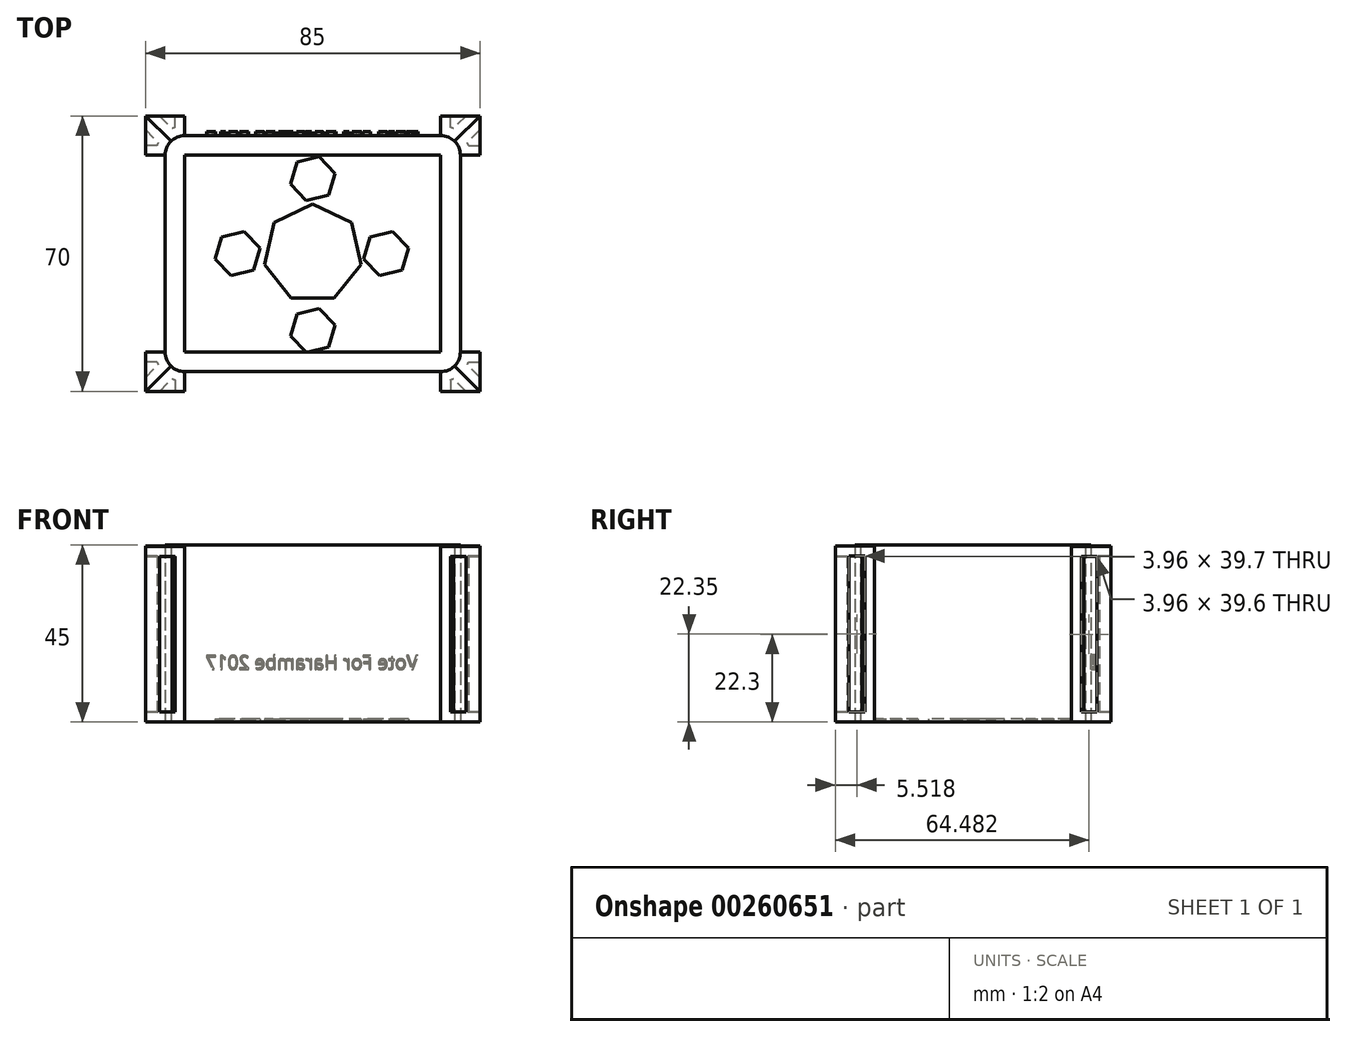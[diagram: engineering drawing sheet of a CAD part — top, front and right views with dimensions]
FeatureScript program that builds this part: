
annotation { "Feature Type Name" : "Feature", "Feature Type Description" : "" }
export const myFeature = defineFeature(function(context is Context, id is Id, definition is map)
    precondition{}
    {
        {
            var Q0;
            Q0=qCreatedBy(makeId("Top.planeOp"),FACE);
            var sketch = newSketch(context, id + "F0", { "sketchPlane" : qUnion([Q0])});
            skLineSegment(sketch, "E0.bottom", {"start": v(32.5, -30) * mm, "end": v(-32.5, -30) * mm});
            skLineSegment(sketch, "E0.top", {"start": v(32.5, 30) * mm, "end": v(-32.5, 30) * mm});
            skLineSegment(sketch, "E0.left", {"start": v(37.5, -25) * mm, "end": v(37.5, 25) * mm});
            skLineSegment(sketch, "E0.right", {"start": v(-37.5, -25) * mm, "end": v(-37.5, 25) * mm});
            skPoint(sketch, "E0.middle", {"position": v(0, 0) * mm});
            skLineSegment(sketch, "E1.bottom", {"start": v(32.5, -25) * mm, "end": v(-32.5, -25) * mm});
            skLineSegment(sketch, "E1.top", {"start": v(32.5, 25) * mm, "end": v(-32.5, 25) * mm});
            skLineSegment(sketch, "E1.left", {"start": v(32.5, -25) * mm, "end": v(32.5, 25) * mm});
            skLineSegment(sketch, "E1.right", {"start": v(-32.5, -25) * mm, "end": v(-32.5, 25) * mm});
            skPoint(sketch, "E2.middle", {"position": v(-37.5, 30) * mm});
            skPoint(sketch, "E3.visualSharp", {"position": v(37.5, 30) * mm});
            skArc(sketch, "E3.filletArc", {"start": v(37.5, 25) * mm, "mid": v(36.04, 28.54) * mm, "end": v(32.5, 30) * mm});
            skPoint(sketch, "E4.visualSharp", {"position": v(37.5, -30) * mm});
            skArc(sketch, "E4.filletArc", {"start": v(32.5, -30) * mm, "mid": v(36.04, -28.54) * mm, "end": v(37.5, -25) * mm});
            skPoint(sketch, "E5.visualSharp", {"position": v(-37.5, -30) * mm});
            skArc(sketch, "E5.filletArc", {"start": v(-37.5, -25) * mm, "mid": v(-36.04, -28.54) * mm, "end": v(-32.5, -30) * mm});
            skArc(sketch, "E6.filletArc", {"start": v(-32.5, 30) * mm, "mid": v(-36.04, 28.54) * mm, "end": v(-37.5, 25) * mm});
            skLineSegment(sketch, "E7.bottom", {"start": v(-32.5, 25) * mm, "end": v(-42.5, 25) * mm});
            skLineSegment(sketch, "E7.top", {"start": v(-32.5, 35) * mm, "end": v(-42.5, 35) * mm});
            skLineSegment(sketch, "E7.left", {"start": v(-32.5, 25) * mm, "end": v(-32.5, 35) * mm});
            skLineSegment(sketch, "E7.right", {"start": v(-42.5, 25) * mm, "end": v(-42.5, 35) * mm});
            skLineSegment(sketch, "E8.bottom", {"start": v(32.5, 25) * mm, "end": v(42.5, 25) * mm});
            skLineSegment(sketch, "E8.top", {"start": v(32.5, 35) * mm, "end": v(42.5, 35) * mm});
            skLineSegment(sketch, "E8.left", {"start": v(32.5, 25) * mm, "end": v(32.5, 35) * mm});
            skLineSegment(sketch, "E8.right", {"start": v(42.5, 25) * mm, "end": v(42.5, 35) * mm});
            skLineSegment(sketch, "E9.bottom", {"start": v(32.5, -25) * mm, "end": v(42.5, -25) * mm});
            skLineSegment(sketch, "E9.top", {"start": v(32.5, -35) * mm, "end": v(42.5, -35) * mm});
            skLineSegment(sketch, "E9.left", {"start": v(32.5, -25) * mm, "end": v(32.5, -35) * mm});
            skLineSegment(sketch, "E9.right", {"start": v(42.5, -25) * mm, "end": v(42.5, -35) * mm});
            skLineSegment(sketch, "E10.bottom", {"start": v(-32.5, -25) * mm, "end": v(-42.5, -25) * mm});
            skLineSegment(sketch, "E10.top", {"start": v(-32.5, -35) * mm, "end": v(-42.5, -35) * mm});
            skLineSegment(sketch, "E10.left", {"start": v(-32.5, -25) * mm, "end": v(-32.5, -35) * mm});
            skLineSegment(sketch, "E10.right", {"start": v(-42.5, -25) * mm, "end": v(-42.5, -35) * mm});
            skLineSegment(sketch, "E11", {"start": v(-42.5, 35) * mm, "end": v(-32.5, 25) * mm});
            skLineSegment(sketch, "E12", {"start": v(42.5, 35) * mm, "end": v(32.5, 25) * mm});
            skLineSegment(sketch, "E13", {"start": v(42.5, -35) * mm, "end": v(32.5, -25) * mm});
            skLineSegment(sketch, "E14", {"start": v(-42.5, -35) * mm, "end": v(-32.5, -25) * mm});
            skSolve(sketch);
        }
        {
            var Q0;
            {var subQ0=sQuery(id+"F0.wireOp",EDGE,"E0.bottom");Q0=makeQuery(id+"F0.imprint","IMPRINT",FACE,{"disambiguationData":[TD([[makeQuery(id+"F0.imprint","IMPRINT",EDGE,{"derivedFrom":subQ0}),-1.0]])]});}
            var Q1;
            {var subQ0=sQuery(id+"F0.wireOp",EDGE,"E0.top");Q1=makeQuery(id+"F0.imprint","IMPRINT",FACE,{"disambiguationData":[TD([[makeQuery(id+"F0.imprint","IMPRINT",EDGE,{"derivedFrom":subQ0}),1.0]])]});}
            var Q2;
            {var subQ0=sQuery(id+"F0.wireOp",EDGE,"E0.left");Q2=makeQuery(id+"F0.imprint","IMPRINT",FACE,{"disambiguationData":[TD([[makeQuery(id+"F0.imprint","IMPRINT",EDGE,{"derivedFrom":subQ0}),1.0]])]});}
            var Q3;
            {var subQ0=sQuery(id+"F0.wireOp",EDGE,"E0.right");Q3=makeQuery(id+"F0.imprint","IMPRINT",FACE,{"disambiguationData":[TD([[makeQuery(id+"F0.imprint","IMPRINT",EDGE,{"derivedFrom":subQ0}),-1.0]])]});}
            var Q4;
            {var subQ1=sQuery(id+"F0.wireOp",EDGE,"E3.filletArc");var subQ3=sQuery(id+"F0.wireOp",EDGE,"E12");var subQ4=makeQuery(id+"F0.imprint","INTERSECT",VERTEX,{"derivedFrom":[subQ1,subQ3]});Q4=makeQuery(id+"F0.imprint","IMPRINT",FACE,{"disambiguationData":[TD([[makeQuery(id+"F0.imprint","IMPRINT",EDGE,{"disambiguationData":[TD([[subQ4,1.0]])],"derivedFrom":subQ1}),1.0]])]});}
            var Q5;
            {var subQ1=sQuery(id+"F0.wireOp",EDGE,"E3.filletArc");var subQ3=sQuery(id+"F0.wireOp",EDGE,"E12");var subQ4=makeQuery(id+"F0.imprint","INTERSECT",VERTEX,{"derivedFrom":[subQ1,subQ3]});Q5=makeQuery(id+"F0.imprint","IMPRINT",FACE,{"disambiguationData":[TD([[makeQuery(id+"F0.imprint","IMPRINT",EDGE,{"disambiguationData":[TD([[subQ4,-1.0]])],"derivedFrom":subQ1}),1.0]])]});}
            var Q6;
            {var subQ1=sQuery(id+"F0.wireOp",EDGE,"E4.filletArc");var subQ3=sQuery(id+"F0.wireOp",EDGE,"E13");var subQ4=makeQuery(id+"F0.imprint","INTERSECT",VERTEX,{"derivedFrom":[subQ1,subQ3]});Q6=makeQuery(id+"F0.imprint","IMPRINT",FACE,{"disambiguationData":[TD([[makeQuery(id+"F0.imprint","IMPRINT",EDGE,{"disambiguationData":[TD([[subQ4,1.0]])],"derivedFrom":subQ1}),1.0]])]});}
            var Q7;
            {var subQ1=sQuery(id+"F0.wireOp",EDGE,"E4.filletArc");var subQ3=sQuery(id+"F0.wireOp",EDGE,"E13");var subQ4=makeQuery(id+"F0.imprint","INTERSECT",VERTEX,{"derivedFrom":[subQ1,subQ3]});Q7=makeQuery(id+"F0.imprint","IMPRINT",FACE,{"disambiguationData":[TD([[makeQuery(id+"F0.imprint","IMPRINT",EDGE,{"disambiguationData":[TD([[subQ4,-1.0]])],"derivedFrom":subQ1}),1.0]])]});}
            var Q8;
            {var subQ1=sQuery(id+"F0.wireOp",EDGE,"E5.filletArc");var subQ3=sQuery(id+"F0.wireOp",EDGE,"E14");var subQ4=makeQuery(id+"F0.imprint","INTERSECT",VERTEX,{"derivedFrom":[subQ1,subQ3]});Q8=makeQuery(id+"F0.imprint","IMPRINT",FACE,{"disambiguationData":[TD([[makeQuery(id+"F0.imprint","IMPRINT",EDGE,{"disambiguationData":[TD([[subQ4,1.0]])],"derivedFrom":subQ1}),1.0]])]});}
            var Q9;
            {var subQ1=sQuery(id+"F0.wireOp",EDGE,"E5.filletArc");var subQ3=sQuery(id+"F0.wireOp",EDGE,"E14");var subQ4=makeQuery(id+"F0.imprint","INTERSECT",VERTEX,{"derivedFrom":[subQ1,subQ3]});Q9=makeQuery(id+"F0.imprint","IMPRINT",FACE,{"disambiguationData":[TD([[makeQuery(id+"F0.imprint","IMPRINT",EDGE,{"disambiguationData":[TD([[subQ4,-1.0]])],"derivedFrom":subQ1}),1.0]])]});}
            var Q10;
            {var subQ1=sQuery(id+"F0.wireOp",EDGE,"E6.filletArc");var subQ3=sQuery(id+"F0.wireOp",EDGE,"E11");var subQ4=makeQuery(id+"F0.imprint","INTERSECT",VERTEX,{"derivedFrom":[subQ1,subQ3]});Q10=makeQuery(id+"F0.imprint","IMPRINT",FACE,{"disambiguationData":[TD([[makeQuery(id+"F0.imprint","IMPRINT",EDGE,{"disambiguationData":[TD([[subQ4,1.0]])],"derivedFrom":subQ1}),1.0]])]});}
            var Q11;
            {var subQ1=sQuery(id+"F0.wireOp",EDGE,"E6.filletArc");var subQ3=sQuery(id+"F0.wireOp",EDGE,"E11");var subQ4=makeQuery(id+"F0.imprint","INTERSECT",VERTEX,{"derivedFrom":[subQ1,subQ3]});Q11=makeQuery(id+"F0.imprint","IMPRINT",FACE,{"disambiguationData":[TD([[makeQuery(id+"F0.imprint","IMPRINT",EDGE,{"disambiguationData":[TD([[subQ4,-1.0]])],"derivedFrom":subQ1}),1.0]])]});}
            extrude(context, id + "F1", {"entities" : qUnion([Q0, Q1, Q2, Q3, Q4, Q5, Q6, Q7, Q8, Q9, Q10, Q11]), "depth" : 45 * mm});
        }
        {
            var Q0;
            Q0=makeQuery(id+"F0.imprint","IMPRINT",FACE,{"disambiguationData":[TD([[makeQuery(id+"F0.imprint","IMPRINT",EDGE,{"derivedFrom":sQuery(id+"F0.wireOp",EDGE,"E1.bottom")}),-1.0]])]});
            extrude(context, id + "F2", {"entities" : qUnion([Q0]), "operationType" : NewBodyOperationType.ADD, "depth" : 0.1 * mm});
        }
        {
            var Q0;
            Q0=makeQuery(id+"F0.imprint","IMPRINT",FACE,{"disambiguationData":[TD([[makeQuery(id+"F0.imprint","IMPRINT",EDGE,{"derivedFrom":sQuery(id+"F0.wireOp",EDGE,"E1.bottom")}),-1.0]])]});
            var sketch = newSketch(context, id + "F3", { "sketchPlane" : qUnion([Q0])});
            skCircle(sketch, "E15.cCircle", {"center": v(0, 0) * mm, "radius": 12.59 * mm, "construction": true});
            skLineSegment(sketch, "E15.0", {"start": v(0, 12.59) * mm, "end": v(9.84, 7.85) * mm});
            skLineSegment(sketch, "E15.1", {"start": v(9.84, 7.85) * mm, "end": v(12.27, -2.8) * mm});
            skLineSegment(sketch, "E15.2", {"start": v(12.27, -2.8) * mm, "end": v(5.46, -11.34) * mm});
            skLineSegment(sketch, "E15.3", {"start": v(5.46, -11.34) * mm, "end": v(-5.46, -11.34) * mm});
            skLineSegment(sketch, "E15.4", {"start": v(-5.46, -11.34) * mm, "end": v(-12.27, -2.8) * mm});
            skLineSegment(sketch, "E15.5", {"start": v(-12.27, -2.8) * mm, "end": v(-9.84, 7.85) * mm});
            skLineSegment(sketch, "E15.6", {"start": v(-9.84, 7.85) * mm, "end": v(0, 12.59) * mm});
            skCircle(sketch, "E16.cCircle", {"center": v(0, 19.03) * mm, "radius": 5.82 * mm, "construction": true});
            skLineSegment(sketch, "E16.0", {"start": v(5.66, 20.4) * mm, "end": v(4.01, 14.81) * mm});
            skLineSegment(sketch, "E16.1", {"start": v(4.01, 14.81) * mm, "end": v(-1.65, 13.44) * mm});
            skLineSegment(sketch, "E16.2", {"start": v(-1.65, 13.44) * mm, "end": v(-5.66, 17.66) * mm});
            skLineSegment(sketch, "E16.3", {"start": v(-5.66, 17.66) * mm, "end": v(-4.01, 23.25) * mm});
            skLineSegment(sketch, "E16.4", {"start": v(-4.01, 23.25) * mm, "end": v(1.65, 24.61) * mm});
            skLineSegment(sketch, "E16.5", {"start": v(1.65, 24.61) * mm, "end": v(5.66, 20.4) * mm});
            skCircle(sketch, "E17.cCircle", {"center": v(-19.1, 0) * mm, "radius": 5.82 * mm, "construction": true});
            skLineSegment(sketch, "E17.0", {"start": v(-13.43, 1.37) * mm, "end": v(-15.08, -4.22) * mm});
            skLineSegment(sketch, "E17.1", {"start": v(-15.08, -4.22) * mm, "end": v(-20.74, -5.58) * mm});
            skLineSegment(sketch, "E17.2", {"start": v(-20.74, -5.58) * mm, "end": v(-24.75, -1.37) * mm});
            skLineSegment(sketch, "E17.3", {"start": v(-24.75, -1.37) * mm, "end": v(-23.1, 4.22) * mm});
            skLineSegment(sketch, "E17.4", {"start": v(-23.1, 4.22) * mm, "end": v(-17.45, 5.58) * mm});
            skLineSegment(sketch, "E17.5", {"start": v(-17.45, 5.58) * mm, "end": v(-13.43, 1.37) * mm});
            skCircle(sketch, "E18.cCircle", {"center": v(18.62, 0) * mm, "radius": 5.82 * mm, "construction": true});
            skLineSegment(sketch, "E18.0", {"start": v(24.28, 1.37) * mm, "end": v(22.63, -4.22) * mm});
            skLineSegment(sketch, "E18.1", {"start": v(22.63, -4.22) * mm, "end": v(16.97, -5.58) * mm});
            skLineSegment(sketch, "E18.2", {"start": v(16.97, -5.58) * mm, "end": v(12.96, -1.37) * mm});
            skLineSegment(sketch, "E18.3", {"start": v(12.96, -1.37) * mm, "end": v(14.6, 4.22) * mm});
            skLineSegment(sketch, "E18.4", {"start": v(14.6, 4.22) * mm, "end": v(20.27, 5.58) * mm});
            skLineSegment(sketch, "E18.5", {"start": v(20.27, 5.58) * mm, "end": v(24.28, 1.37) * mm});
            skCircle(sketch, "E19.cCircle", {"center": v(0, -19.53) * mm, "radius": 5.82 * mm, "construction": true});
            skLineSegment(sketch, "E19.0", {"start": v(5.66, -18.16) * mm, "end": v(4.01, -23.75) * mm});
            skLineSegment(sketch, "E19.1", {"start": v(4.01, -23.75) * mm, "end": v(-1.65, -25.11) * mm});
            skLineSegment(sketch, "E19.2", {"start": v(-1.65, -25.11) * mm, "end": v(-5.66, -20.9) * mm});
            skLineSegment(sketch, "E19.3", {"start": v(-5.66, -20.9) * mm, "end": v(-4.01, -15.3) * mm});
            skLineSegment(sketch, "E19.4", {"start": v(-4.01, -15.3) * mm, "end": v(1.65, -13.94) * mm});
            skLineSegment(sketch, "E19.5", {"start": v(1.65, -13.94) * mm, "end": v(5.66, -18.16) * mm});
            skPoint(sketch, "E20.startSnap0", {"position": v(-4.92, 10.22) * mm});
            skLineSegment(sketch, "E21", {"start": v(12.27, -2.8) * mm, "end": v(32.75, -24.92) * mm});
            skLineSegment(sketch, "E22", {"start": v(-32.32, -24.75) * mm, "end": v(-12.27, -2.8) * mm});
            skLineSegment(sketch, "E23", {"start": v(-9.84, 7.85) * mm, "end": v(-32.32, 25.03) * mm});
            skLineSegment(sketch, "E24", {"start": v(9.84, 7.85) * mm, "end": v(32.43, 25.03) * mm});
            skSolve(sketch);
        }
        {
            var Q0;
            Q0 = qSketchRegion(id + "F3", true);
            extrude(context, id + "F4", {"entities" : qUnion([Q0]), "operationType" : NewBodyOperationType.ADD, "depth" : 0.8 * mm});
        }
        {
            var Q0;
            {var subQ5=sQuery(id+"F0.wireOp",EDGE,"E7.right");Q0=makeQuery(id+"F0.imprint","IMPRINT",FACE,{"disambiguationData":[TD([[makeQuery(id+"F0.imprint","IMPRINT",EDGE,{"derivedFrom":subQ5}),-1.0]])]});}
            var Q1;
            {var subQ5=sQuery(id+"F0.wireOp",EDGE,"E10.top");Q1=makeQuery(id+"F0.imprint","IMPRINT",FACE,{"disambiguationData":[TD([[makeQuery(id+"F0.imprint","IMPRINT",EDGE,{"derivedFrom":subQ5}),-1.0]])]});}
            var Q2;
            {var subQ5=sQuery(id+"F0.wireOp",EDGE,"E8.right");Q2=makeQuery(id+"F0.imprint","IMPRINT",FACE,{"disambiguationData":[TD([[makeQuery(id+"F0.imprint","IMPRINT",EDGE,{"derivedFrom":subQ5}),1.0]])]});}
            var Q3;
            {var subQ5=sQuery(id+"F0.wireOp",EDGE,"E9.top");Q3=makeQuery(id+"F0.imprint","IMPRINT",FACE,{"disambiguationData":[TD([[makeQuery(id+"F0.imprint","IMPRINT",EDGE,{"derivedFrom":subQ5}),1.0]])]});}
            extrude(context, id + "F5", {"entities" : qUnion([Q0, Q1, Q2, Q3]), "depth" : 44.6 * mm});
        }
        {
            var Q0;
            {var subQ5=sQuery(id+"F0.wireOp",EDGE,"E10.right");Q0=makeQuery(id+"F0.imprint","IMPRINT",FACE,{"disambiguationData":[TD([[makeQuery(id+"F0.imprint","IMPRINT",EDGE,{"derivedFrom":subQ5}),1.0]])]});}
            var Q1;
            {var subQ5=sQuery(id+"F0.wireOp",EDGE,"E9.right");Q1=makeQuery(id+"F0.imprint","IMPRINT",FACE,{"disambiguationData":[TD([[makeQuery(id+"F0.imprint","IMPRINT",EDGE,{"derivedFrom":subQ5}),-1.0]])]});}
            var Q2;
            {var subQ5=sQuery(id+"F0.wireOp",EDGE,"E8.top");Q2=makeQuery(id+"F0.imprint","IMPRINT",FACE,{"disambiguationData":[TD([[makeQuery(id+"F0.imprint","IMPRINT",EDGE,{"derivedFrom":subQ5}),-1.0]])]});}
            var Q3;
            {var subQ5=sQuery(id+"F0.wireOp",EDGE,"E7.top");Q3=makeQuery(id+"F0.imprint","IMPRINT",FACE,{"disambiguationData":[TD([[makeQuery(id+"F0.imprint","IMPRINT",EDGE,{"derivedFrom":subQ5}),1.0]])]});}
            extrude(context, id + "F6", {"entities" : qUnion([Q0, Q1, Q2, Q3]), "depth" : 44.7 * mm});
        }
        {
            var Q0;
            Q0=makeQuery(id+"F5.opExtrude","SWEPT_FACE",FACE,{"disambiguationData":[OSD([sQuery(id+"F0.wireOp",EDGE,"E10.top")])]});
            var Q1;
            Q1=makeQuery(id+"F6.opExtrude","SWEPT_FACE",FACE,{"disambiguationData":[OSD([sQuery(id+"F0.wireOp",EDGE,"E10.right")])]});
            var Q2;
            Q2=makeQuery(id+"F5.opExtrude","SWEPT_FACE",FACE,{"disambiguationData":[OSD([sQuery(id+"F0.wireOp",EDGE,"E9.top")])]});
            var Q3;
            Q3=makeQuery(id+"F6.opExtrude","SWEPT_FACE",FACE,{"disambiguationData":[OSD([sQuery(id+"F0.wireOp",EDGE,"E9.right")])]});
            var Q4;
            Q4=makeQuery(id+"F5.opExtrude","SWEPT_FACE",FACE,{"disambiguationData":[OSD([sQuery(id+"F0.wireOp",EDGE,"E8.right")])]});
            var Q5;
            Q5=makeQuery(id+"F6.opExtrude","SWEPT_FACE",FACE,{"disambiguationData":[OSD([sQuery(id+"F0.wireOp",EDGE,"E8.top")])]});
            var Q6;
            Q6=makeQuery(id+"F6.opExtrude","SWEPT_FACE",FACE,{"disambiguationData":[OSD([sQuery(id+"F0.wireOp",EDGE,"E7.top")])]});
            var Q7;
            Q7=makeQuery(id+"F5.opExtrude","SWEPT_FACE",FACE,{"disambiguationData":[OSD([sQuery(id+"F0.wireOp",EDGE,"E7.right")])]});
            shell(context, id + "F7", {"entities" : qUnion([Q0, Q1, Q2, Q3, Q4, Q5, Q6, Q7]), "thickness" : 2.5 * mm});
        }
        {
            var Q0;
            Q0=makeQuery(id+"F1.opExtrude","SWEPT_FACE",FACE,{"disambiguationData":[OSD([sQuery(id+"F0.wireOp",EDGE,"E0.top")])]});
            var sketch = newSketch(context, id + "F8", { "sketchPlane" : qUnion([Q0])});
            skText(sketch, "E25", { "text": "Vote For Harambe 2017", "fontName": "OpenSans-Regular.ttf"});
            const initialGuessF8  = {"E25": [-0.02674, 0.01337, 1, 0, 0.00351]};
            skSetInitialGuess(sketch, initialGuessF8);
            skSolve(sketch);
        }
        {
            var Q0;
            Q0 = qSketchRegion(id + "F8", true);
            extrude(context, id + "F9", {"entities" : qUnion([Q0]), "operationType" : NewBodyOperationType.ADD, "depth" : 1 * mm});
        }
    });
